# Revit family: Лифт_Пассажирский_МетеорЛифт_NeoClassic_LOD100
name_source: partatom
category: Оборудование
units: mm (PartAtom-declared; Revit-internal decimal feet)

## family parameters
Всегда вертикально = Да
Общий = Да
При загрузке вырезать с полостями = Да
Размер круглого соединителя = Использовать диаметр
Тип детали = Нормальный
Точка расчета площади = Нет

## types (8) — shared parameters
CAGOVLOC 1 = Нет
CAGOVLOC 4 = Нет
URL = https://meteor.ru
Изготовитель = ООО "Метеор Лифт"
Накладное = Объемная панель
Описание = Лифт электрический пассажирский с машинным помещением
Телефон = 8 800 200 68 47
zero-valued in all types: Отметка по умолчанию

## per-type parameters (varying)
| type | CAGOVLOC | CAGOVLOC 2 | CAGOVLOC 3 | CARDBG | CD | CW | CWTLOC | CWTLOC_12 | CWTLOC_13 | DL | NBPAS | TCLOC | X_CWT | Y_CWT | Количество пассажиров | Привязка отверстия для ПК | Привязка переднего фасада кабины | Расположение противовеса | Тип кабины |
| Г/п 1000 кг / Кабина 2100х1100 (ШхГ) / Противовес сзади | 3 | Нет | Да | 2180 мм | 1100 мм | 2100 мм | 12 | Да | Нет | 1000 | 13 | 2 | 775 мм | 200 мм | 13 | 830 мм | 480 мм | Сзади | 13X |
| Г/п 400 кг / Кабина 1100х950 (ШхГ) / Противовес сзади | 2 | Да | Нет | 1180 мм | 950 мм | 1100 мм | 12 | Да | Нет | 400 | 5 | 1 | 665 мм | 0 мм | 5 | 435 мм | 440 мм | Сзади | 05W |
| Г/п 630 кг / Кабина 1100х1400 (ШхГ) / Противовес сбоку | 3 | Нет | Да | 1180 мм | 1400 мм | 1100 мм | 13 | Нет | Да | 630 | 8 | 2 | 395 мм | 750 мм | 8 | 715 мм | 600 мм | Сбоку | 08D |
| Г/п 1000 кг / Кабина 1100х2100 (ШхГ) / Противовес сбоку | 3 | Нет | Да | 1180 мм | 2100 мм | 1100 мм | 13 | Нет | Да | 1000 | 13 | 3 | 560 мм | 740 мм | 13 | 750 мм | 920 мм | Сбоку | 13D |
| Г/п 1000 кг / Кабина 1600х1400 (ШхГ) / Противовес сзади | 3 | Нет | Да | 1680 мм | 1400 мм | 1600 мм | 12 | Да | Нет | 1000 | 13 | 2 | 960 мм | 200 мм | 13 | 475 мм | 600 мм | Сзади | 13W |
| Г/п 630 кг / Кабина 2100х1100 (ШхГ) / Противовес сзади | 3 | Нет | Да | 2180 мм | 1100 мм | 2100 мм | 12 | Да | Нет | 630 | 8 | 2 | 775 мм | 200 мм | 8 | 830 мм | 480 мм | Сзади | 08X |
| Г/п 630 кг / Кабина 1100х2100 (ШхГ) / Противовес сбоку | 3 | Нет | Да | 1180 мм | 2100 мм | 1100 мм | 13 | Нет | Да | 630 | 8 | 3 | 560 мм | 740 мм | 8 | 750 мм | 920 мм | Сбоку | L08 |
| Г/п 630 кг / Кабина 1100х1400 (ШхГ) / Противовес сзади | 3 | Нет | Да | 1180 мм | 1400 мм | 1100 мм | 12 | Да | Нет | 630 | 8 | 2 | 960 мм | 200 мм | 8 | 475 мм | 600 мм | Сзади | 08D |

## geometry (parser evidence)
native form markers: Sweep x3
no freeform markers — native parametric forms only
